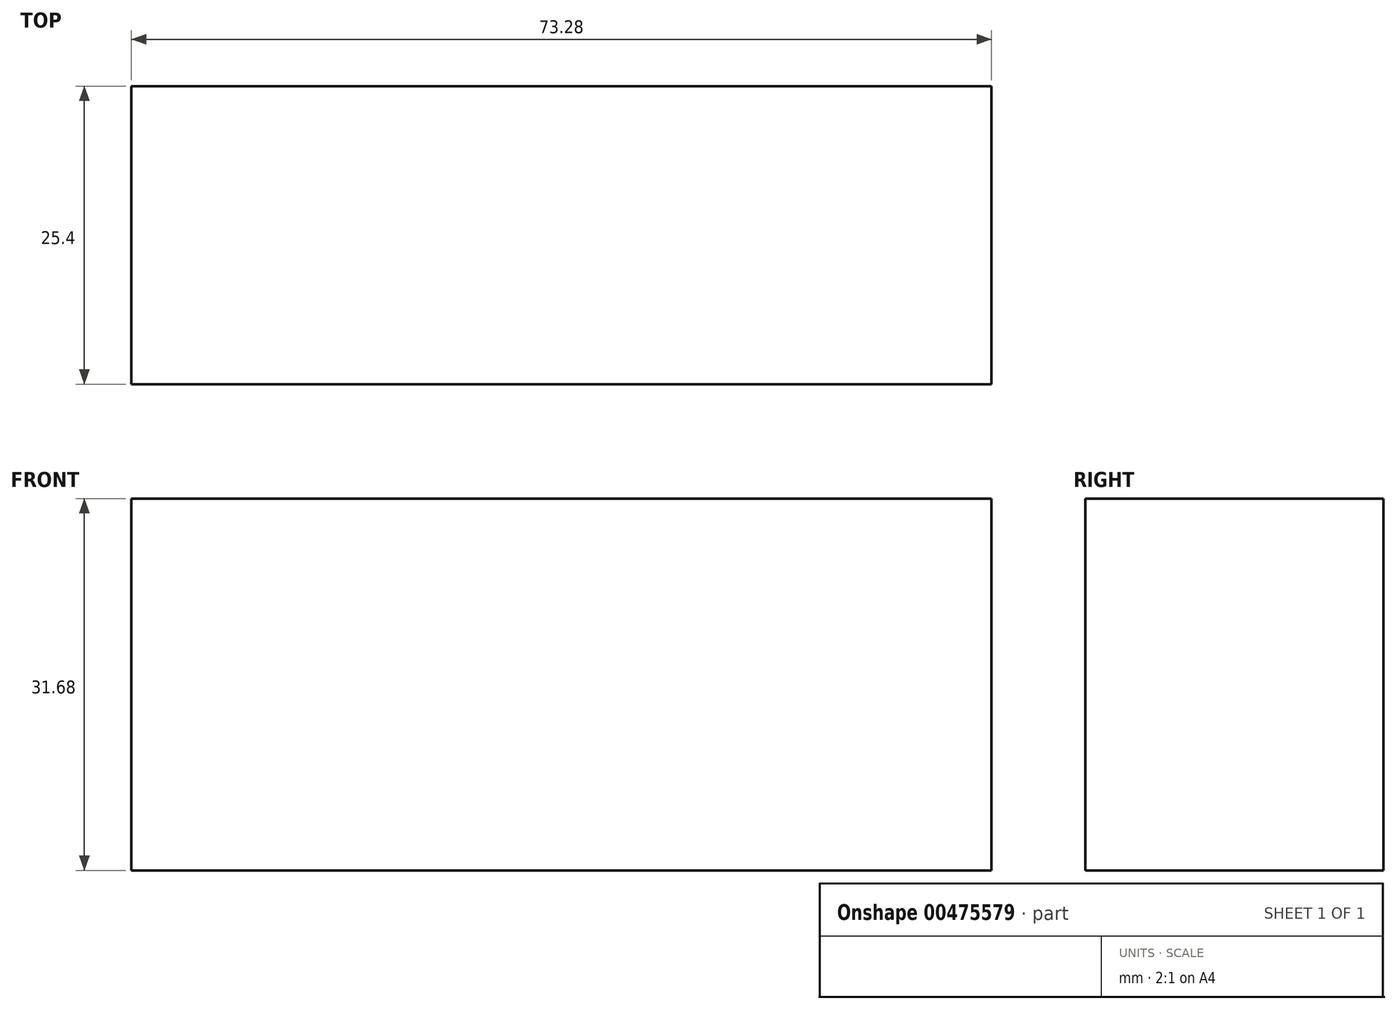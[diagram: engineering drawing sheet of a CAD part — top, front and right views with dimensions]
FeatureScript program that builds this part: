
annotation { "Feature Type Name" : "Feature", "Feature Type Description" : "" }
export const myFeature = defineFeature(function(context is Context, id is Id, definition is map)
    precondition{}
    {
        {
            var Q0;
            Q0=qCreatedBy(makeId("Front.planeOp"),FACE);
            var sketch = newSketch(context, id + "F0", { "sketchPlane" : qUnion([Q0])});
            skLineSegment(sketch, "E0.bottom", {"start": v(-36.64, 15.84) * mm, "end": v(36.64, 15.84) * mm});
            skLineSegment(sketch, "E0.top", {"start": v(-36.64, -15.84) * mm, "end": v(36.64, -15.84) * mm});
            skLineSegment(sketch, "E0.left", {"start": v(-36.64, 15.84) * mm, "end": v(-36.64, -15.84) * mm});
            skLineSegment(sketch, "E0.right", {"start": v(36.64, 15.84) * mm, "end": v(36.64, -15.84) * mm});
            skPoint(sketch, "E0.middle", {"position": v(0, 0) * mm});
            skSolve(sketch);
        }
        {
            var Q0;
            Q0=makeQuery(id+"F0.imprint","IMPRINT",FACE,{"disambiguationData":[TD([[makeQuery(id+"F0.imprint","IMPRINT",EDGE,{"derivedFrom":sQuery(id+"F0.wireOp",EDGE,"E0.bottom")}),-1.0]])]});
            extrude(context, id + "F1", {"entities" : qUnion([Q0]), "depth" : 25.4 * mm});
        }
    });
